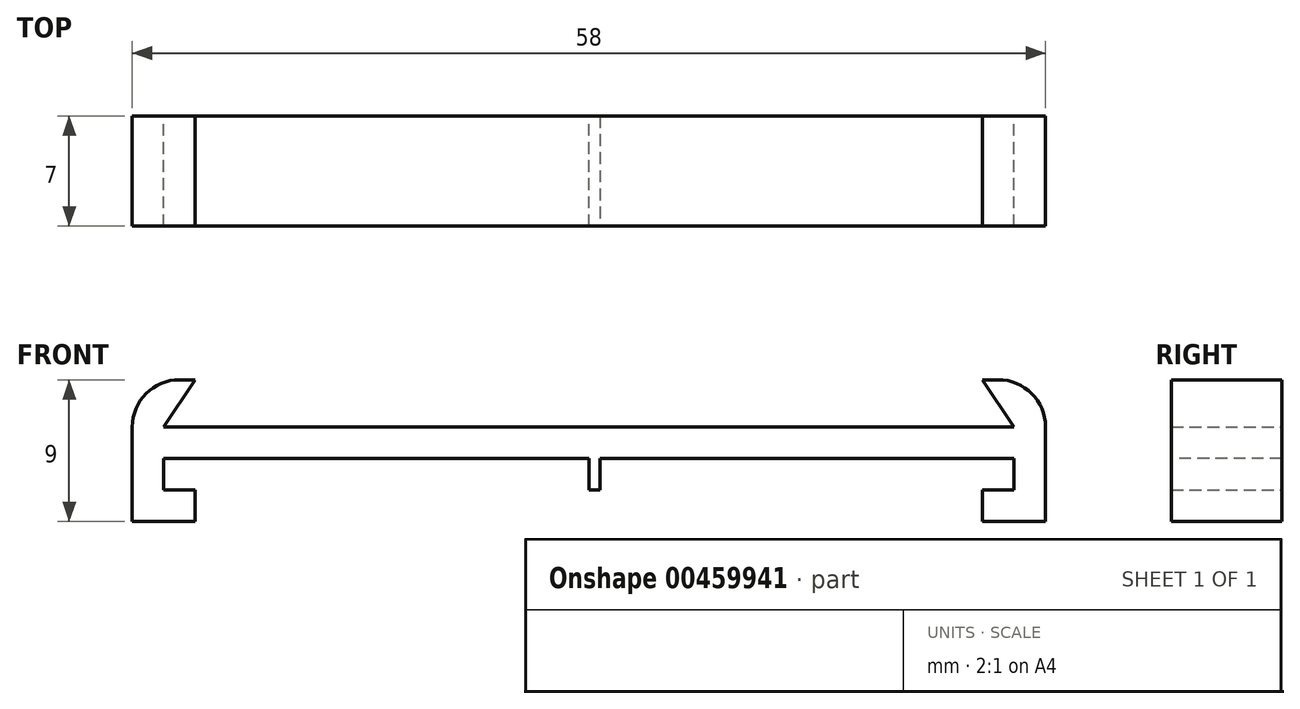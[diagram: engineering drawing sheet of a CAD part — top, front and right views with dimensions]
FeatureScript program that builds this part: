
annotation { "Feature Type Name" : "Feature", "Feature Type Description" : "" }
export const myFeature = defineFeature(function(context is Context, id is Id, definition is map)
    precondition{}
    {
        {
            var Q0;
            Q0=qCreatedBy(makeId("Front.planeOp"),FACE);
            var sketch = newSketch(context, id + "F0", { "sketchPlane" : qUnion([Q0])});
            skLineSegment(sketch, "E0", {"start": v(0, 6) * mm, "end": v(58, 6) * mm});
            skLineSegment(sketch, "E1", {"start": v(58, 6) * mm, "end": v(58, 0) * mm});
            skLineSegment(sketch, "E2", {"start": v(58, 0) * mm, "end": v(54, 0) * mm});
            skLineSegment(sketch, "E3", {"start": v(54, 0) * mm, "end": v(54, 2) * mm});
            skLineSegment(sketch, "E4", {"start": v(54, 2) * mm, "end": v(56, 2) * mm});
            skLineSegment(sketch, "E5", {"start": v(56, 2) * mm, "end": v(56, 4) * mm});
            skLineSegment(sketch, "E6", {"start": v(56, 4) * mm, "end": v(2, 4) * mm});
            skLineSegment(sketch, "E7", {"start": v(2, 4) * mm, "end": v(2, 2) * mm});
            skLineSegment(sketch, "E8", {"start": v(2, 2) * mm, "end": v(4, 2) * mm});
            skLineSegment(sketch, "E9", {"start": v(4, 2) * mm, "end": v(4, 0) * mm});
            skLineSegment(sketch, "E10", {"start": v(4, 0) * mm, "end": v(0, 0) * mm});
            skLineSegment(sketch, "E11", {"start": v(0, 0) * mm, "end": v(0, 6) * mm});
            skLineSegment(sketch, "E12", {"start": v(0, 6) * mm, "end": v(0, 9) * mm});
            skLineSegment(sketch, "E13", {"start": v(0, 9) * mm, "end": v(4, 9) * mm});
            skLineSegment(sketch, "E14", {"start": v(4, 9) * mm, "end": v(2, 6) * mm});
            skLineSegment(sketch, "E15", {"start": v(58, 6) * mm, "end": v(58, 9) * mm});
            skLineSegment(sketch, "E16", {"start": v(58, 9) * mm, "end": v(54, 9) * mm});
            skLineSegment(sketch, "E17", {"start": v(54, 9) * mm, "end": v(56, 6) * mm});
            skSolve(sketch);
        }
        {
            var Q0;
            Q0 = qSketchRegion(id + "F0", true);
            extrude(context, id + "F1", {"entities" : qUnion([Q0]), "depth" : 7 * mm});
        }
        {
            var Q0;
            Q0=makeQuery(id+"F1.opExtrude","SWEPT_EDGE",EDGE,{"disambiguationData":[OSD([sQuery(id+"F0.wireOp",EDGE,"E12"),sQuery(id+"F0.wireOp",EDGE,"E13")])]});
            var Q1;
            Q1=makeQuery(id+"F1.opExtrude","SWEPT_EDGE",EDGE,{"disambiguationData":[OSD([sQuery(id+"F0.wireOp",EDGE,"E15"),sQuery(id+"F0.wireOp",EDGE,"E16")])]});
            fillet(context, id + "F2", {"entities" : qUnion([Q0, Q1]), "radius" : 3 * mm, "tangentPropagation" : true, "allowEdgeOverflow" : false});
        }
        {
            var Q0;
            Q0=makeQuery(id+"F1.opExtrude","SWEPT_FACE",FACE,{"disambiguationData":[OSD([sQuery(id+"F0.wireOp",EDGE,"E6")])]});
            var sketch = newSketch(context, id + "F3", { "sketchPlane" : qUnion([Q0])});
            skLineSegment(sketch, "E18", {"start": v(29, 7) * mm, "end": v(29, 0) * mm});
            skLineSegment(sketch, "E19", {"start": v(29.7, 0) * mm, "end": v(29, 0) * mm});
            skLineSegment(sketch, "E20", {"start": v(29.7, 0) * mm, "end": v(29.7, 7) * mm});
            skLineSegment(sketch, "E21", {"start": v(29, 7) * mm, "end": v(29.7, 7) * mm});
            skSolve(sketch);
        }
        {
            var Q0;
            Q0 = qSketchRegion(id + "F3", true);
            extrude(context, id + "F4", {"entities" : qUnion([Q0]), "operationType" : NewBodyOperationType.ADD, "depth" : 2 * mm});
        }
    });
